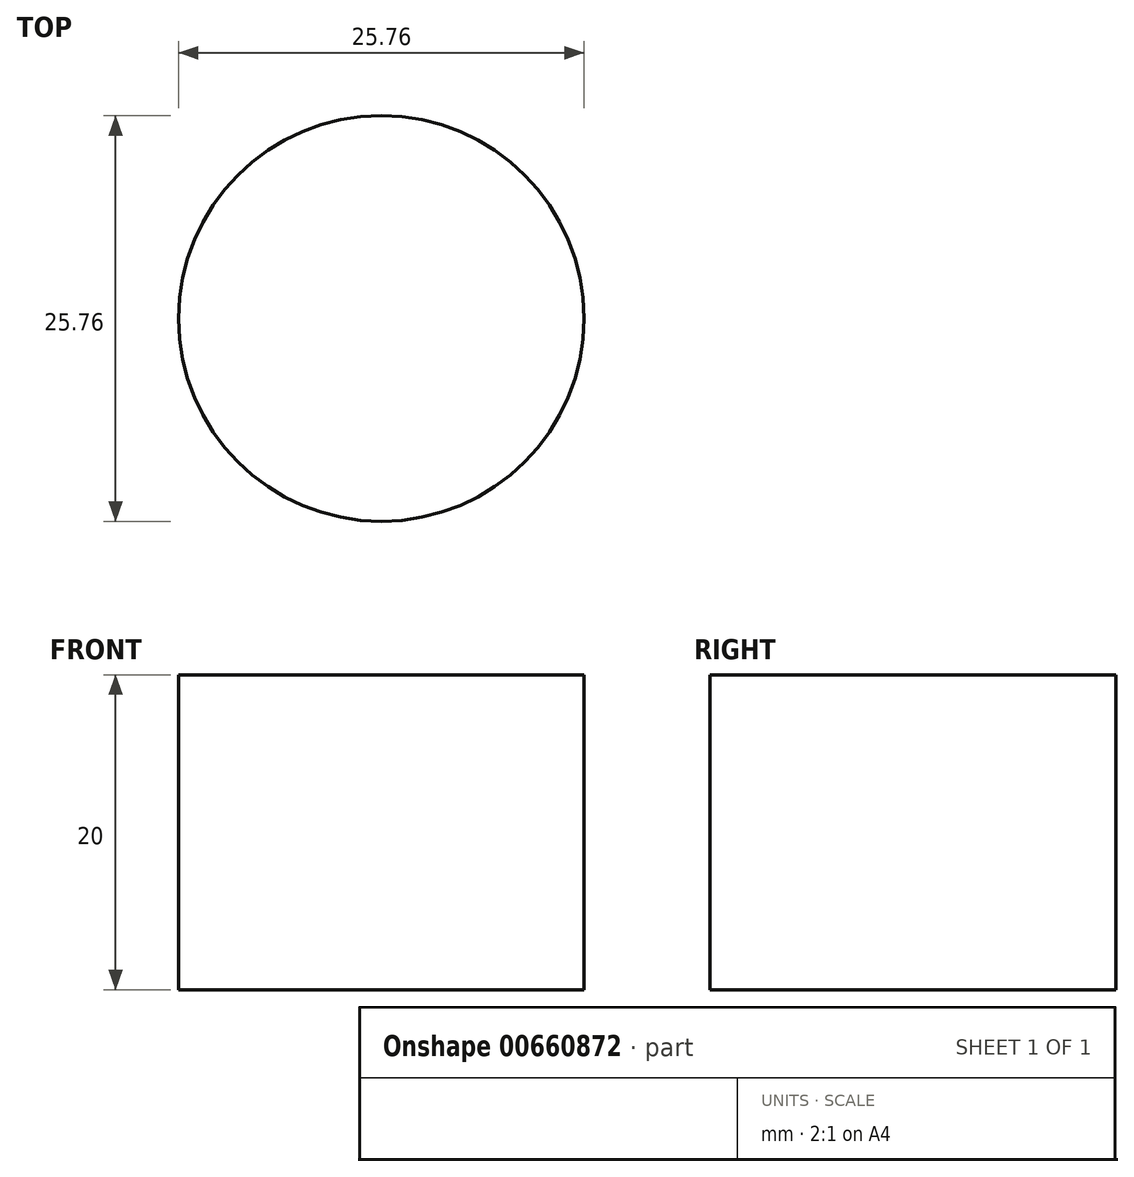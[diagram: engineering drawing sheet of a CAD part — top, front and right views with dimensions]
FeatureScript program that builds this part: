
annotation { "Feature Type Name" : "Feature", "Feature Type Description" : "" }
export const myFeature = defineFeature(function(context is Context, id is Id, definition is map)
    precondition{}
    {
        {
            var Q0;
            Q0=qCreatedBy(makeId("Top.planeOp"),FACE);
            var sketch = newSketch(context, id + "F0", { "sketchPlane" : qUnion([Q0])});
            skCircle(sketch, "E0", {"center": v(0, 0) * mm, "radius": 12.88 * mm});
            skSolve(sketch);
        }
        {
            var Q0;
            Q0 = qSketchRegion(id + "F0", true);
            var Q1;
            Q1=makeQuery(id+"F0.imprint","IMPRINT",FACE,{"disambiguationData":[TD([[makeQuery(id+"F0.imprint","IMPRINT",EDGE,{"derivedFrom":sQuery(id+"F0.wireOp",EDGE,"E0")}),1.0]])]});
            extrude(context, id + "F1", {"entities" : qUnion([Q0, Q1]), "depth" : 20 * mm, "offsetDistance" : 25 * mm});
        }
        {
            var Q0;
            Q0=makeQuery(id+"F1.opExtrude","CAP_FACE",FACE,{"disambiguationData":[OSD([sQuery(id+"F0.wireOp",EDGE,"E0")])],"isStart":false});
            cPlane(context, id + "F2", {"entities" : qUnion([Q0]), "cplaneType" : CPlaneType.OFFSET, "offset" : 5 * mm, "width" : 150 * mm, "height" : 150 * mm});
        }
    });
